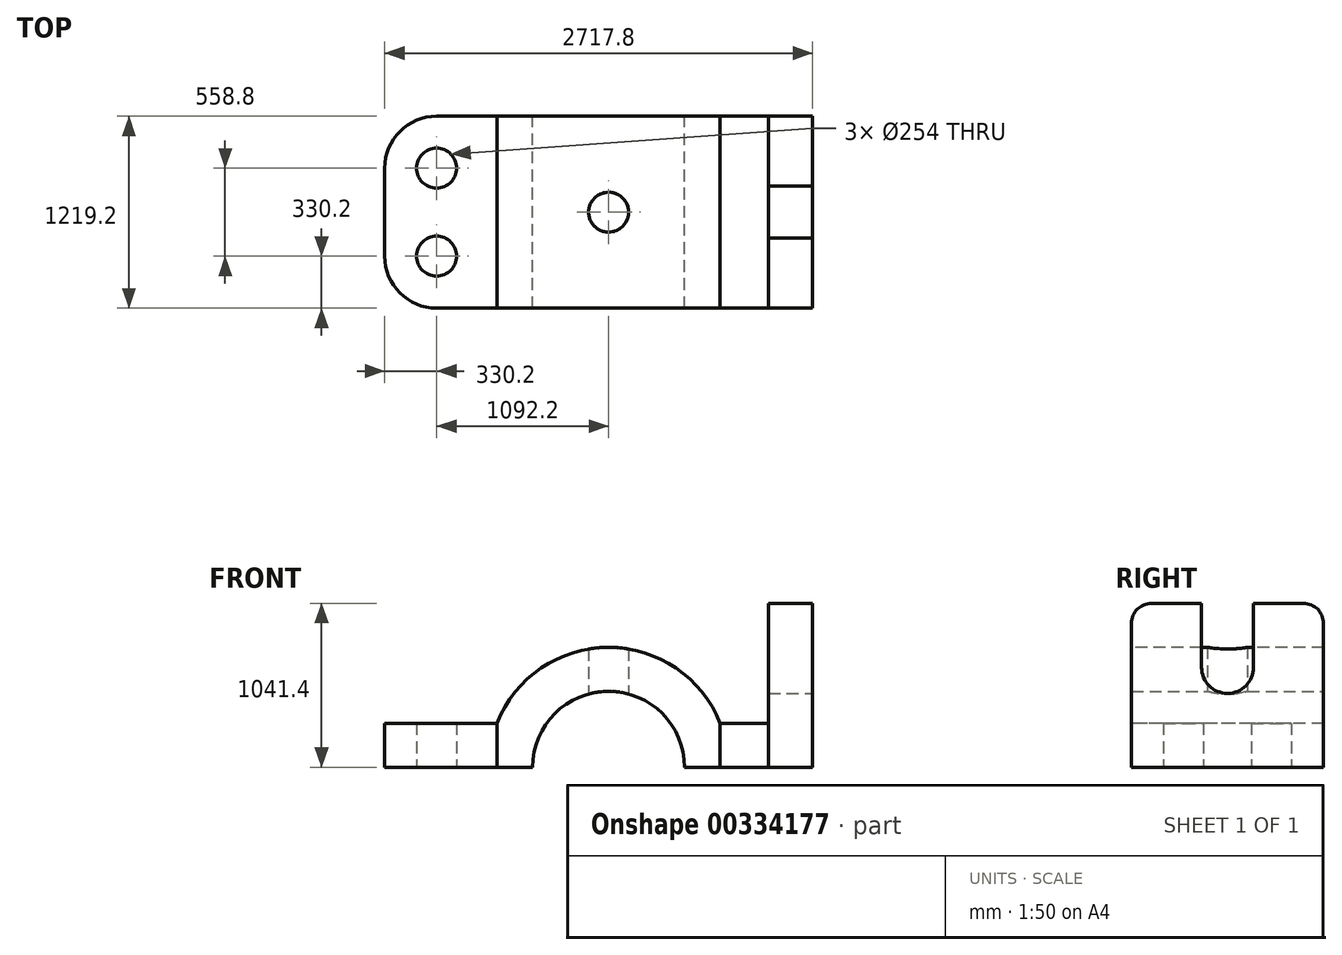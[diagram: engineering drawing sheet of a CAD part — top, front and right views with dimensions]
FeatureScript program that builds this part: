
annotation { "Feature Type Name" : "Feature", "Feature Type Description" : "" }
export const myFeature = defineFeature(function(context is Context, id is Id, definition is map)
    precondition{}
    {
        {
            var Q0;
            Q0=qCreatedBy(makeId("Right.planeOp"),FACE);
            cPlane(context, id + "F0", {"entities" : qUnion([Q0]), "cplaneType" : CPlaneType.OFFSET, "offset" : 1193.8 * mm, "width" : 152.4 * mm, "height" : 152.4 * mm});
        }
        {
            var Q0;
            Q0=qCreatedBy(makeId("Top.planeOp"),FACE);
            var sketch = newSketch(context, id + "F1", { "sketchPlane" : qUnion([Q0])});
            skLineSegment(sketch, "E0.bottom", {"start": v(1193.8, 609.6) * mm, "end": v(-1193.8, 609.6) * mm});
            skLineSegment(sketch, "E0.top", {"start": v(1193.8, -609.6) * mm, "end": v(-1193.8, -609.6) * mm});
            skLineSegment(sketch, "E0.left", {"start": v(1193.8, 609.6) * mm, "end": v(1193.8, -609.6) * mm});
            skPoint(sketch, "E0.middle", {"position": v(0, 0) * mm});
            skArc(sketch, "E1", {"start": v(-1193.8, 609.6) * mm, "mid": v(-1427.29, 512.89) * mm, "end": v(-1524, 279.4) * mm});
            skArc(sketch, "E2", {"start": v(-1193.8, -609.6) * mm, "mid": v(-1427.29, -512.89) * mm, "end": v(-1524, -279.4) * mm});
            skLineSegment(sketch, "E3", {"start": v(-1524, 279.4) * mm, "end": v(-1524, -279.4) * mm});
            skCircle(sketch, "E4", {"center": v(-1193.8, -279.4) * mm, "radius": 127 * mm});
            skCircle(sketch, "E5", {"center": v(-1193.8, 279.4) * mm, "radius": 127 * mm});
            skLineSegment(sketch, "E6", {"start": v(-810.53, -609.6) * mm, "end": v(-810.53, 609.6) * mm});
            skLineSegment(sketch, "E7", {"start": v(914.4, 609.6) * mm, "end": v(914.4, -609.6) * mm});
            skLineSegment(sketch, "E8", {"start": v(660.4, 609.6) * mm, "end": v(660.4, -609.6) * mm});
            skLineSegment(sketch, "E9", {"start": v(914.4, 165.1) * mm, "end": v(1193.8, 165.1) * mm});
            skLineSegment(sketch, "E10", {"start": v(914.4, -165.1) * mm, "end": v(1193.8, -165.1) * mm});
            skCircle(sketch, "E11", {"center": v(-101.6, 0) * mm, "radius": 127 * mm});
            skCircle(sketch, "E12", {"center": v(-101.6, 0) * mm, "radius": 63.5 * mm});
            skLineSegment(sketch, "E13", {"start": v(607.33, 609.6) * mm, "end": v(607.33, -609.6) * mm});
            skSolve(sketch);
        }
        {
            var Q0;
            Q0=qCreatedBy(makeId("Front.planeOp"),FACE);
            var sketch = newSketch(context, id + "F2", { "sketchPlane" : qUnion([Q0])});
            skCircle(sketch, "E14", {"center": v(-101.6, 0) * mm, "radius": 762 * mm});
            skCircle(sketch, "E15", {"center": v(-101.6, 0) * mm, "radius": 482.6 * mm});
            skLineSegment(sketch, "E16.bottom", {"start": v(-101.6, 0) * mm, "end": v(660.4, 0) * mm});
            skLineSegment(sketch, "E16.top", {"start": v(-101.6, 762) * mm, "end": v(660.4, 762) * mm});
            skLineSegment(sketch, "E16.left", {"start": v(-101.6, 0) * mm, "end": v(-101.6, 762) * mm});
            skLineSegment(sketch, "E16.right", {"start": v(660.4, 0) * mm, "end": v(660.4, 762) * mm});
            skLineSegment(sketch, "E17.bottom", {"start": v(-101.6, 762) * mm, "end": v(-863.6, 762) * mm});
            skLineSegment(sketch, "E17.top", {"start": v(-101.6, 0) * mm, "end": v(-863.6, 0) * mm});
            skLineSegment(sketch, "E17.left", {"start": v(-101.6, 762) * mm, "end": v(-101.6, 0) * mm});
            skLineSegment(sketch, "E17.right", {"start": v(-863.6, 762) * mm, "end": v(-863.6, 0) * mm});
            skSolve(sketch);
        }
        {
            var Q0;
            {var subQ7=sQuery(id+"F1.wireOp",EDGE,"E8");Q0=makeQuery(id+"F1.imprint","IMPRINT",FACE,{"disambiguationData":[TD([[makeQuery(id+"F1.imprint","IMPRINT",EDGE,{"derivedFrom":subQ7}),1.0]])]});}
            var Q1;
            {var subQ0=sQuery(id+"F1.wireOp",EDGE,"E8");Q1=makeQuery(id+"F1.imprint","IMPRINT",FACE,{"disambiguationData":[TD([[makeQuery(id+"F1.imprint","IMPRINT",EDGE,{"derivedFrom":subQ0}),-1.0]])]});}
            extrude(context, id + "F3", {"entities" : qUnion([Q0, Q1]), "depth" : 279.4 * mm});
        }
        {
            var Q0;
            {var subQ5=sQuery(id+"F1.wireOp",EDGE,"E9");Q0=makeQuery(id+"F1.imprint","IMPRINT",FACE,{"disambiguationData":[TD([[makeQuery(id+"F1.imprint","IMPRINT",EDGE,{"derivedFrom":subQ5}),1.0]])]});}
            var Q1;
            {var subQ0=sQuery(id+"F1.wireOp",EDGE,"E9");Q1=makeQuery(id+"F1.imprint","IMPRINT",FACE,{"disambiguationData":[TD([[makeQuery(id+"F1.imprint","IMPRINT",EDGE,{"derivedFrom":subQ0}),-1.0]])]});}
            var Q2;
            {var subQ5=sQuery(id+"F1.wireOp",EDGE,"E10");Q2=makeQuery(id+"F1.imprint","IMPRINT",FACE,{"disambiguationData":[TD([[makeQuery(id+"F1.imprint","IMPRINT",EDGE,{"derivedFrom":subQ5}),-1.0]])]});}
            extrude(context, id + "F4", {"entities" : qUnion([Q0, Q1, Q2]), "depth" : 1041.4 * mm});
        }
        {
            var Q0;
            {var subQ1=sQuery(id+"F1.wireOp",EDGE,"E6");Q0=makeQuery(id+"F1.imprint","IMPRINT",FACE,{"disambiguationData":[TD([[makeQuery(id+"F1.imprint","IMPRINT",EDGE,{"derivedFrom":subQ1}),-1.0]])]});}
            extrude(context, id + "F5", {"entities" : qUnion([Q0]), "depth" : 762 * mm});
        }
        {
            var Q0;
            {var subQ0=sQuery(id+"F1.wireOp",EDGE,"E1");Q0=makeQuery(id+"F1.imprint","IMPRINT",FACE,{"disambiguationData":[TD([[makeQuery(id+"F1.imprint","IMPRINT",EDGE,{"derivedFrom":subQ0}),1.0]])]});}
            extrude(context, id + "F6", {"entities" : qUnion([Q0]), "depth" : 279.4 * mm});
        }
        {
            var Q0;
            Q0=makeQuery(id+"F2.imprint","IMPRINT",FACE,{"disambiguationData":[TD([[makeQuery(id+"F2.imprint","IMPRINT",EDGE,{"derivedFrom":sQuery(id+"F2.wireOp",EDGE,"E15")}),1.0]])]});
            extrude(context, id + "F7", {"entities" : qUnion([Q0]), "operationType" : NewBodyOperationType.REMOVE, "endBound" : BoundingType.SYMMETRIC, "depth" : 30480 * mm});
        }
        {
            var Q0;
            Q0=qCreatedBy(makeId("Front.planeOp"),FACE);
            var sketch = newSketch(context, id + "F8", { "sketchPlane" : qUnion([Q0])});
            skArc(sketch, "E18", {"start": v(660.4, 0) * mm, "mid": v(-101.6, 762) * mm, "end": v(-863.6, 0) * mm});
            skLineSegment(sketch, "E19.bottom", {"start": v(-810.53, 279.4) * mm, "end": v(607.33, 279.4) * mm});
            skLineSegment(sketch, "E19.top", {"start": v(-810.53, 762) * mm, "end": v(607.33, 762) * mm});
            skLineSegment(sketch, "E19.left", {"start": v(-810.53, 279.4) * mm, "end": v(-810.53, 762) * mm});
            skLineSegment(sketch, "E19.right", {"start": v(607.33, 279.4) * mm, "end": v(607.33, 762) * mm});
            skSolve(sketch);
        }
        {
            var Q0;
            {var subQ0=sQuery(id+"F8.wireOp",EDGE,"E19.left");Q0=makeQuery(id+"F8.imprint","IMPRINT",FACE,{"disambiguationData":[TD([[makeQuery(id+"F8.imprint","IMPRINT",EDGE,{"derivedFrom":subQ0}),-1.0]])]});}
            var Q1;
            {var subQ0=sQuery(id+"F8.wireOp",EDGE,"E19.right");Q1=makeQuery(id+"F8.imprint","IMPRINT",FACE,{"disambiguationData":[TD([[makeQuery(id+"F8.imprint","IMPRINT",EDGE,{"derivedFrom":subQ0}),1.0]])]});}
            extrude(context, id + "F9", {"entities" : qUnion([Q0, Q1]), "operationType" : NewBodyOperationType.REMOVE, "endBound" : BoundingType.SYMMETRIC, "oppositeDirection" : true, "depth" : 279400 * mm});
        }
        {
            var Q0;
            Q0=qCreatedBy(id+"F0.planeOp",FACE);
            var sketch = newSketch(context, id + "F10", { "sketchPlane" : qUnion([Q0])});
            skArc(sketch, "E20", {"start": v(-609.6, 914.4) * mm, "mid": v(-572.4, 1004.2) * mm, "end": v(-482.6, 1041.4) * mm});
            skLineSegment(sketch, "E21", {"start": v(-609.6, 895.91) * mm, "end": v(-609.6, 1041.4) * mm});
            skLineSegment(sketch, "E22", {"start": v(-482.6, 1041.4) * mm, "end": v(-609.6, 1041.4) * mm});
            skArc(sketch, "E23", {"start": v(609.6, 914.4) * mm, "mid": v(572.4, 1004.2) * mm, "end": v(482.6, 1041.4) * mm});
            skLineSegment(sketch, "E24.bottom", {"start": v(-165.1, 1041.4) * mm, "end": v(165.1, 1041.4) * mm});
            skLineSegment(sketch, "E24.left", {"start": v(-165.1, 1041.4) * mm, "end": v(-165.1, 635) * mm});
            skLineSegment(sketch, "E24.right", {"start": v(165.1, 1041.4) * mm, "end": v(165.1, 635) * mm});
            skArc(sketch, "E25", {"start": v(165.1, 635) * mm, "mid": v(0, 469.9) * mm, "end": v(-165.1, 635) * mm});
            skLineSegment(sketch, "E26.bottom", {"start": v(482.6, 1041.4) * mm, "end": v(609.6, 1041.4) * mm});
            skLineSegment(sketch, "E26.right", {"start": v(609.6, 1041.4) * mm, "end": v(609.6, 914.4) * mm});
            skLineSegment(sketch, "E27", {"start": v(609.6, 1041.4) * mm, "end": v(482.6, 1041.4) * mm});
            skSolve(sketch);
        }
        {
            var Q0;
            Q0 = qSketchRegion(id + "F10", true);
            extrude(context, id + "F11", {"entities" : qUnion([Q0]), "operationType" : NewBodyOperationType.REMOVE, "oppositeDirection" : true, "depth" : 279.4 * mm});
        }
    });
